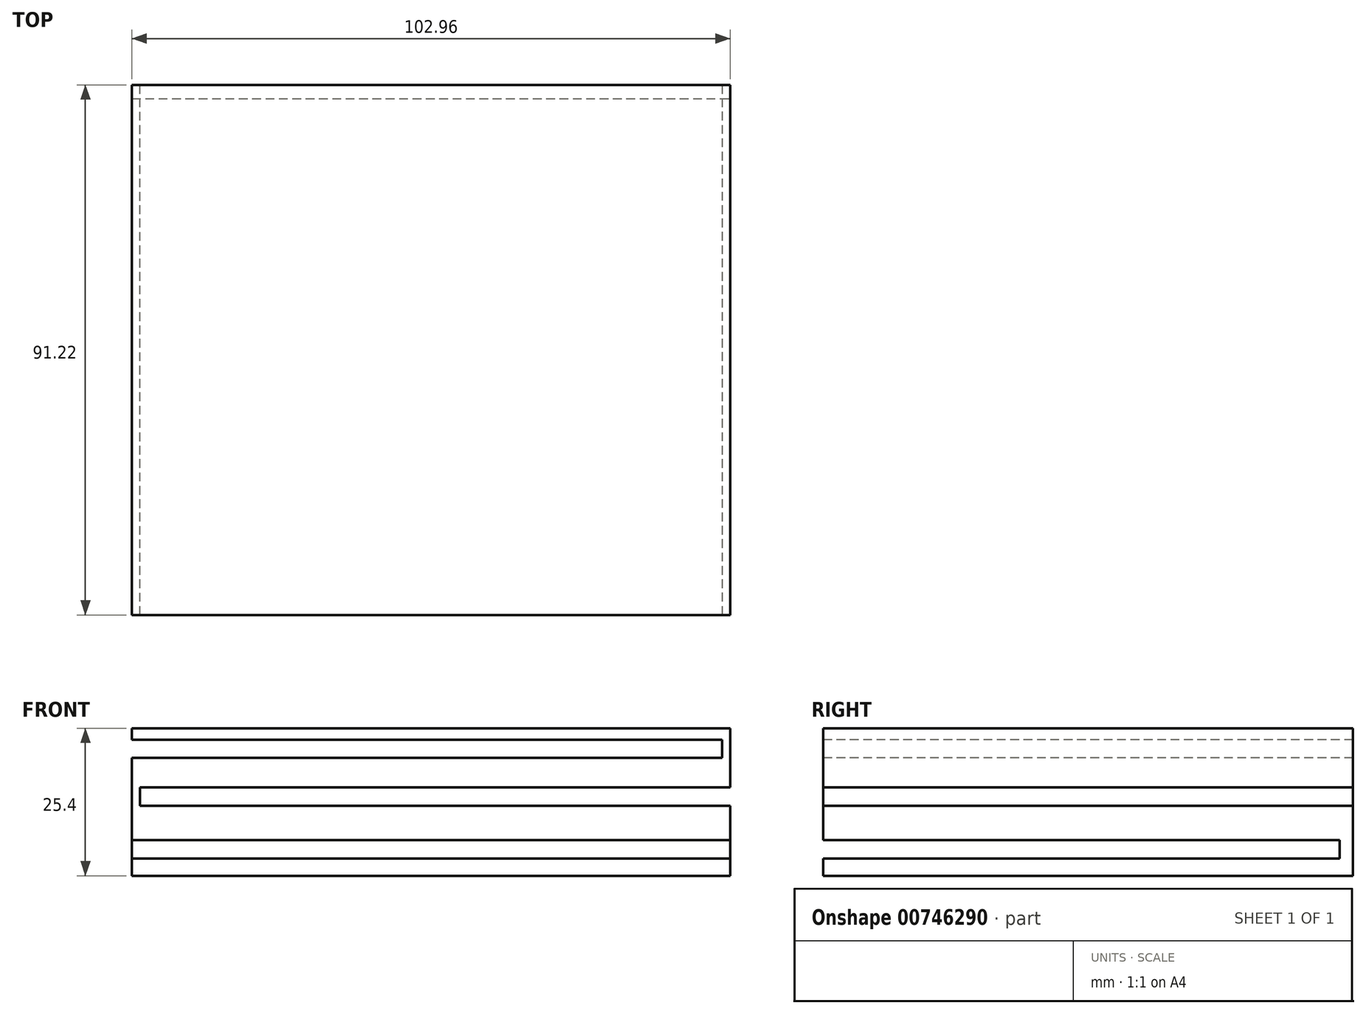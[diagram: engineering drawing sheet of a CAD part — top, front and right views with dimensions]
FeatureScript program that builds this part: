
annotation { "Feature Type Name" : "Feature", "Feature Type Description" : "" }
export const myFeature = defineFeature(function(context is Context, id is Id, definition is map)
    precondition{}
    {
        {
            var Q0;
            Q0=qCreatedBy(makeId("Top.planeOp"),FACE);
            var sketch = newSketch(context, id + "F0", { "sketchPlane" : qUnion([Q0])});
            skLineSegment(sketch, "E0.bottom", {"start": v(51.48, -45.61) * mm, "end": v(-51.48, -45.61) * mm});
            skLineSegment(sketch, "E0.top", {"start": v(51.48, 45.61) * mm, "end": v(-51.48, 45.61) * mm});
            skLineSegment(sketch, "E0.left", {"start": v(51.48, -45.61) * mm, "end": v(51.48, 45.61) * mm});
            skLineSegment(sketch, "E0.right", {"start": v(-51.48, -45.61) * mm, "end": v(-51.48, 45.61) * mm});
            skPoint(sketch, "E0.middle", {"position": v(0, 0) * mm});
            skSolve(sketch);
        }
        {
            var Q0;
            Q0=makeQuery(id+"F0.imprint","IMPRINT",FACE,{"disambiguationData":[TD([[makeQuery(id+"F0.imprint","IMPRINT",EDGE,{"derivedFrom":sQuery(id+"F0.wireOp",EDGE,"E0.bottom")}),-1.0]])]});
            extrude(context, id + "F1", {"entities" : qUnion([Q0]), "depth" : 25.4 * mm, "offsetDistance" : 25.4 * mm});
        }
        {
            var Q0;
            Q0=makeQuery(id+"F1.opExtrude","SWEPT_FACE",FACE,{"disambiguationData":[OSD([sQuery(id+"F0.wireOp",EDGE,"E0.right")])]});
            var sketch = newSketch(context, id + "F2", { "sketchPlane" : qUnion([Q0])});
            skLineSegment(sketch, "E1.bottom", {"start": v(-45.61, 23.4) * mm, "end": v(45.61, 23.4) * mm});
            skLineSegment(sketch, "E1.top", {"start": v(-45.61, 20.28) * mm, "end": v(45.61, 20.28) * mm});
            skLineSegment(sketch, "E1.left", {"start": v(-45.61, 23.4) * mm, "end": v(-45.61, 20.28) * mm});
            skLineSegment(sketch, "E1.right", {"start": v(45.61, 23.4) * mm, "end": v(45.61, 20.28) * mm});
            skSolve(sketch);
        }
        {
            var Q0;
            Q0=makeQuery(id+"F2.imprint","IMPRINT",FACE,{"disambiguationData":[TD([[makeQuery(id+"F2.imprint","IMPRINT",EDGE,{"derivedFrom":sQuery(id+"F2.wireOp",EDGE,"E1.bottom")}),-1.0]])]});
            extrude(context, id + "F3", {"entities" : qUnion([Q0]), "operationType" : NewBodyOperationType.REMOVE, "oppositeDirection" : true, "depth" : 101.6 * mm, "offsetDistance" : 25.4 * mm});
        }
        {
            var Q0;
            Q0=makeQuery(id+"F1.opExtrude","SWEPT_FACE",FACE,{"disambiguationData":[OSD([sQuery(id+"F0.wireOp",EDGE,"E0.left")])]});
            var sketch = newSketch(context, id + "F4", { "sketchPlane" : qUnion([Q0])});
            skLineSegment(sketch, "E2.bottom", {"start": v(-45.61, 12.06) * mm, "end": v(45.61, 12.06) * mm});
            skLineSegment(sketch, "E2.top", {"start": v(-45.61, 15.24) * mm, "end": v(45.61, 15.24) * mm});
            skLineSegment(sketch, "E2.left", {"start": v(-45.61, 15.24) * mm, "end": v(-45.61, 12.06) * mm});
            skLineSegment(sketch, "E2.right", {"start": v(45.61, 15.24) * mm, "end": v(45.61, 12.06) * mm});
            skSolve(sketch);
        }
        {
            var Q0;
            Q0=makeQuery(id+"F4.imprint","IMPRINT",FACE,{"disambiguationData":[TD([[makeQuery(id+"F4.imprint","IMPRINT",EDGE,{"derivedFrom":sQuery(id+"F4.wireOp",EDGE,"E2.bottom")}),1.0]])]});
            extrude(context, id + "F5", {"entities" : qUnion([Q0]), "operationType" : NewBodyOperationType.REMOVE, "oppositeDirection" : true, "depth" : 101.6 * mm, "offsetDistance" : 25.4 * mm});
        }
        {
            var Q0;
            Q0=makeQuery(id+"F1.opExtrude","SWEPT_FACE",FACE,{"disambiguationData":[OSD([sQuery(id+"F0.wireOp",EDGE,"E0.bottom")])]});
            var sketch = newSketch(context, id + "F6", { "sketchPlane" : qUnion([Q0])});
            skLineSegment(sketch, "E3.bottom", {"start": v(-51.48, 6.12) * mm, "end": v(51.48, 6.12) * mm});
            skLineSegment(sketch, "E3.top", {"start": v(-51.48, 2.94) * mm, "end": v(51.48, 2.94) * mm});
            skLineSegment(sketch, "E3.left", {"start": v(-51.48, 6.12) * mm, "end": v(-51.48, 2.94) * mm});
            skLineSegment(sketch, "E3.right", {"start": v(51.48, 6.12) * mm, "end": v(51.48, 2.94) * mm});
            skSolve(sketch);
        }
        {
            var Q0;
            Q0=makeQuery(id+"F6.imprint","IMPRINT",FACE,{"disambiguationData":[TD([[makeQuery(id+"F6.imprint","IMPRINT",EDGE,{"derivedFrom":sQuery(id+"F6.wireOp",EDGE,"E3.bottom")}),-1.0]])]});
            extrude(context, id + "F7", {"entities" : qUnion([Q0]), "operationType" : NewBodyOperationType.REMOVE, "oppositeDirection" : true, "depth" : 88.9 * mm, "offsetDistance" : 25.4 * mm});
        }
    });
